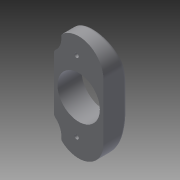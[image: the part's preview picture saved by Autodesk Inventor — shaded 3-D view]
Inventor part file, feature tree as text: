
AUTODESK INVENTOR PART (.ipt)
format: ipt  version: 2015 (Build 190159000, 159)  size: 256,000 bytes
history: native  units: mm
features: extrude x4, sketch x4, fillet x2, chamfer x1
ambient origin geometry x8: Origin, YZ Plane, XZ Plane, XY Plane, X Axis, Y Axis, Z Axis, Center Point
bodies: Solid1 (feature_tree)
feature tree (11):
  extrude  "Extrusion1"  Depth=75.0mm
  extrude  "Extrusion2"  Depth=3.0mm
  extrude  "Extrusion3"  Depth=17.0mm TaperAngle=0.0deg
  fillet  "Fillet1"  Radius=30.0mm
  extrude  "Extrusion4"  Depth=10.0mm
  fillet  "Fillet2"  Radius=35.0mm
  chamfer  "Chamfer1"  Distance=35.0mm
  sketch  "Sketch1"  dims[d0=35.0mm d1=75.0mm]
  sketch  "Sketch2"  dims[d2=30.0mm d7=3.0mm]
  sketch  "Sketch3"  dims[d8=3.0mm d9=17.0mm d10=0.0mm d12=30.0mm]
  sketch  "Sketch4"  dims[d13=10.0mm d14=10.0mm d15=35.0mm d16=0.0mm d17=35.0mm d18=40.0mm d19=17.0mm d20=0.0mm d21=35.0mm d26=12.0mm d27=12.0mm d28=17.0mm d29=0.0mm d30=2.5mm d31=0.7mm d32=2.0mm d33=45.0deg d34=19.0mm d35=19.0mm]
